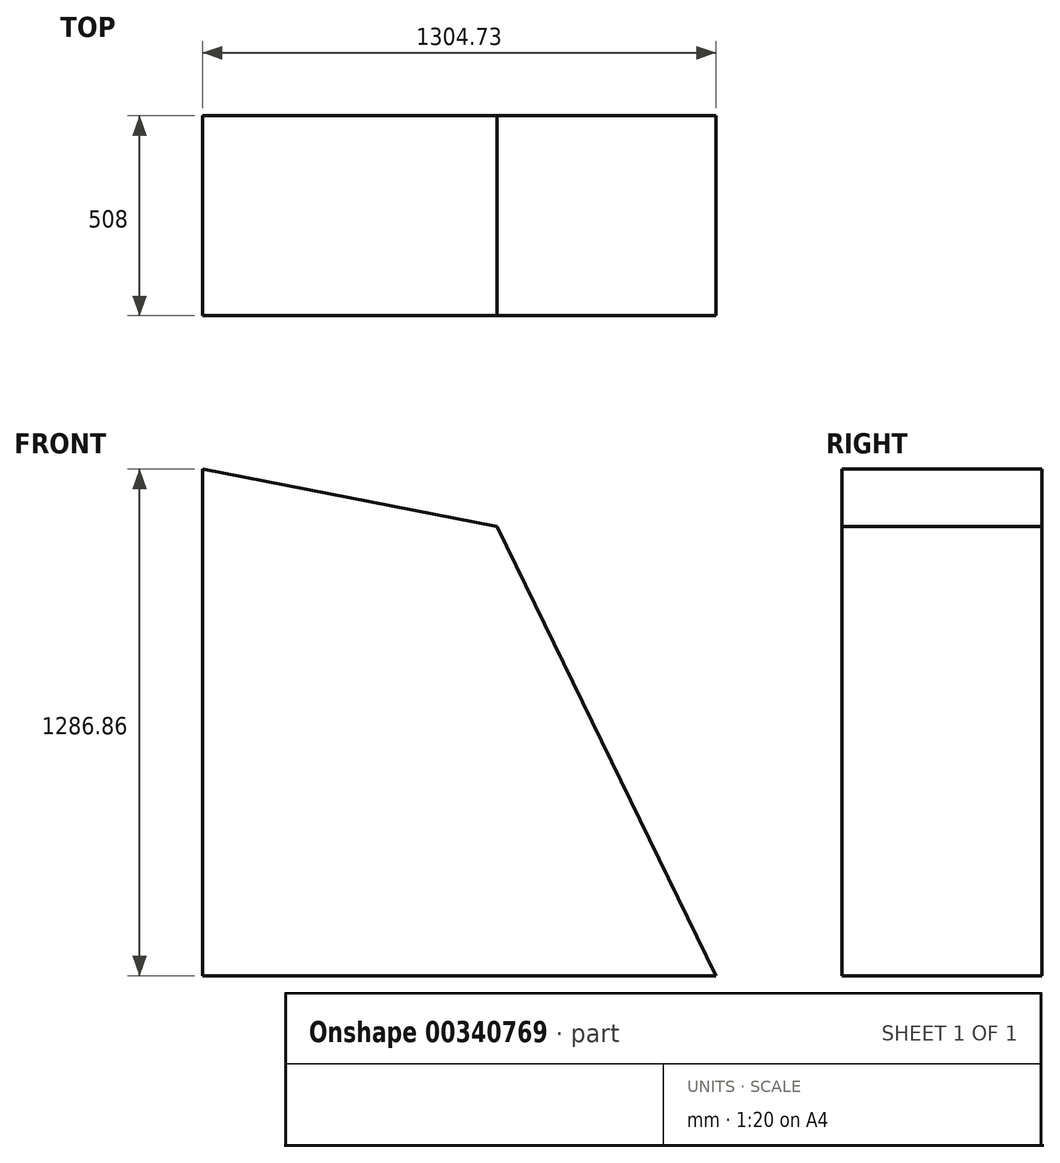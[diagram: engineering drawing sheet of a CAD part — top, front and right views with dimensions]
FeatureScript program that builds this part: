
annotation { "Feature Type Name" : "Feature", "Feature Type Description" : "" }
export const myFeature = defineFeature(function(context is Context, id is Id, definition is map)
    precondition{}
    {
        {
            var Q0;
            Q0=qCreatedBy(makeId("Front.planeOp"),FACE);
            var sketch = newSketch(context, id + "F0", { "sketchPlane" : qUnion([Q0])});
            skLineSegment(sketch, "E0", {"start": v(-748, 1014.72) * mm, "end": v(-748, -272.14) * mm});
            skLineSegment(sketch, "E1", {"start": v(-748, -272.14) * mm, "end": v(556.73, -272.14) * mm});
            skLineSegment(sketch, "E2", {"start": v(556.73, -272.14) * mm, "end": v(0, 869.33) * mm});
            skLineSegment(sketch, "E3", {"start": v(0, 869.33) * mm, "end": v(-748, 1014.72) * mm});
            skSolve(sketch);
        }
        {
            var Q0;
            Q0=makeQuery(id+"F0.imprint","IMPRINT",FACE,{"disambiguationData":[TD([[makeQuery(id+"F0.imprint","IMPRINT",EDGE,{"derivedFrom":sQuery(id+"F0.wireOp",EDGE,"E0")}),1.0]])]});
            extrude(context, id + "F1", {"entities" : qUnion([Q0]), "depth" : 508 * mm});
        }
    });
